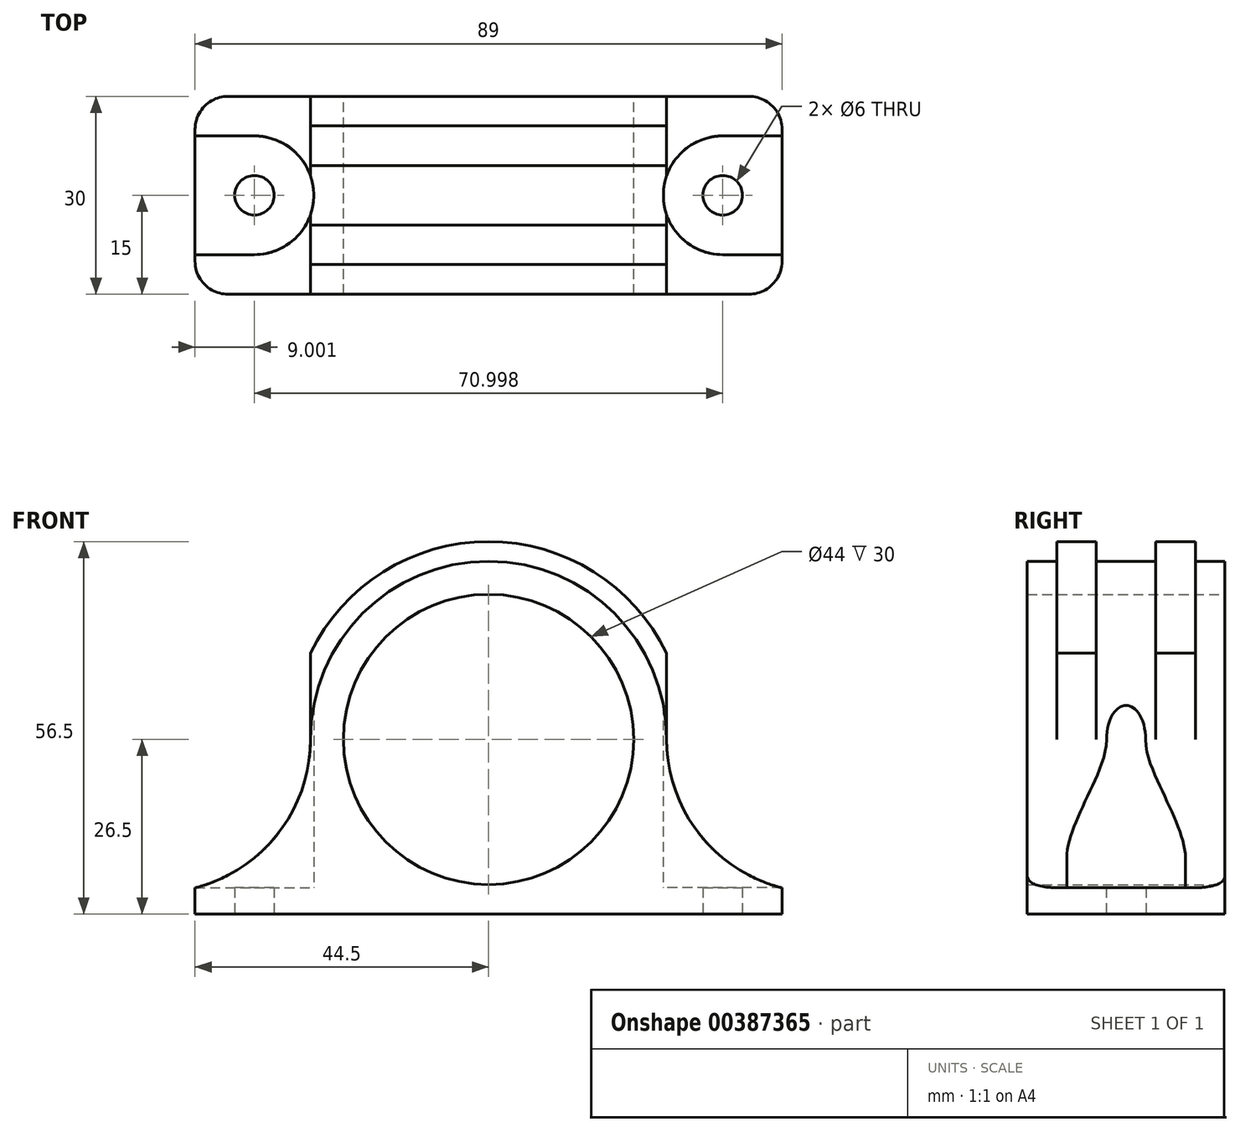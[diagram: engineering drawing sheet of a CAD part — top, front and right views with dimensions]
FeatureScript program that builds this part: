
annotation { "Feature Type Name" : "Feature", "Feature Type Description" : "" }
export const myFeature = defineFeature(function(context is Context, id is Id, definition is map)
    precondition{}
    {
        {
            var Q0;
            Q0=qCreatedBy(makeId("Front.planeOp"),FACE);
            var sketch = newSketch(context, id + "F0", { "sketchPlane" : qUnion([Q0])});
            skPoint(sketch, "E0", {"position": v(0, 0) * mm});
            skLineSegment(sketch, "E1", {"start": v(0, 0) * mm, "end": v(0, -26.5) * mm, "construction": true});
            skLineSegment(sketch, "E2", {"start": v(0, -26.5) * mm, "end": v(35.5, -26.5) * mm, "construction": true});
            skCircle(sketch, "E3", {"center": v(0, 0) * mm, "radius": 22 * mm, "construction": true});
            skLineSegment(sketch, "E4", {"start": v(35.5, -26.5) * mm, "end": v(44.5, -26.5) * mm, "construction": true});
            skLineSegment(sketch, "E5", {"start": v(44.5, -26.5) * mm, "end": v(0, -26.5) * mm});
            skLineSegment(sketch, "E6", {"start": v(35.5, -26.5) * mm, "end": v(26.5, -26.5) * mm, "construction": true});
            skArc(sketch, "E7", {"start": v(0, 22) * mm, "mid": v(22, 0) * mm, "end": v(0, -22) * mm});
            skLineSegment(sketch, "E8", {"start": v(0, -26.5) * mm, "end": v(0, -22) * mm});
            skLineSegment(sketch, "E9", {"start": v(44.5, -26.5) * mm, "end": v(44.5, -24.5) * mm, "construction": true});
            skLineSegment(sketch, "E10", {"start": v(44.5, -26.5) * mm, "end": v(44.5, -24.5) * mm});
            skPoint(sketch, "E11.snap10", {"position": v(17.75, -26.5) * mm});
            skLineSegment(sketch, "E12", {"start": v(44.5, -24.5) * mm, "end": v(44.5, -22.5) * mm});
            skLineSegment(sketch, "E13", {"start": v(0, 22) * mm, "end": v(0, 27) * mm, "construction": true});
            skPoint(sketch, "E14", {"position": v(0, 24.5) * mm});
            skArc(sketch, "E15", {"start": v(0, 27) * mm, "mid": v(25.85, 7.8) * mm, "end": v(14.92, -22.5) * mm, "construction": true});
            skLineSegment(sketch, "E16", {"start": v(22, 0) * mm, "end": v(24.5, 0) * mm, "construction": true});
            skArc(sketch, "E17", {"start": v(0, 27) * mm, "mid": v(19.1, 19.1) * mm, "end": v(27, 0) * mm});
            skLineSegment(sketch, "E18", {"start": v(22, 0) * mm, "end": v(24.5, 0) * mm});
            skLineSegment(sketch, "E19", {"start": v(24.5, 0) * mm, "end": v(24.5, -24.5) * mm});
            skLineSegment(sketch, "E20", {"start": v(24.5, -24.5) * mm, "end": v(44.5, -24.5) * mm});
            skLineSegment(sketch, "E21", {"start": v(44.5, -22.5) * mm, "end": v(24.5, -22.5) * mm, "construction": true});
            skLineSegment(sketch, "E22", {"start": v(27, 0) * mm, "end": v(27, -22.5) * mm});
            skLineSegment(sketch, "E23", {"start": v(27, -22.5) * mm, "end": v(44.5, -22.5) * mm});
            skLineSegment(sketch, "E24", {"start": v(0, 27) * mm, "end": v(0, 22) * mm});
            skArc(sketch, "E25", {"start": v(27, 0) * mm, "mid": v(31.9, -14.25) * mm, "end": v(44.5, -22.5) * mm});
            skSolve(sketch);
        }
        {
            var Q0;
            Q0=makeQuery(id+"F0.imprint","IMPRINT",FACE,{"disambiguationData":[TD([[makeQuery(id+"F0.imprint","IMPRINT",EDGE,{"derivedFrom":sQuery(id+"F0.wireOp",EDGE,"E5")}),-1.0]])]});
            extrude(context, id + "F1", {"entities" : qUnion([Q0]), "depth" : 15 * mm, "offsetDistance" : 25 * mm, "hasSecondDirection" : true, "secondDirectionOppositeDirection" : true, "secondDirectionDepth" : 15 * mm});
        }
        {
            var Q0;
            Q0=makeQuery(id+"F0.imprint","IMPRINT",FACE,{"disambiguationData":[TD([[makeQuery(id+"F0.imprint","IMPRINT",EDGE,{"derivedFrom":sQuery(id+"F0.wireOp",EDGE,"E12")}),1.0]])]});
            var Q1;
            Q1=makeQuery(id+"F0.imprint","IMPRINT",FACE,{"disambiguationData":[TD([[makeQuery(id+"F0.imprint","IMPRINT",EDGE,{"derivedFrom":sQuery(id+"F0.wireOp",EDGE,"E22")}),1.0]])]});
            extrude(context, id + "F2", {"entities" : qUnion([Q0, Q1]), "depth" : 15 * mm, "offsetDistance" : 25 * mm, "hasSecondDirection" : true, "secondDirectionOppositeDirection" : true, "secondDirectionDepth" : 15 * mm});
        }
        {
            var Q0;
            Q0=makeQuery(id+"F1.opExtrude","SWEPT_FACE",FACE,{"disambiguationData":[OSD([sQuery(id+"F0.wireOp",EDGE,"E5")])]});
            var sketch = newSketch(context, id + "F3", { "sketchPlane" : qUnion([Q0])});
            skPoint(sketch, "E26", {"position": v(35.5, 0) * mm});
            skPoint(sketch, "E26.positionSnap0", {"position": v(44.5, 0) * mm});
            skCircle(sketch, "E27", {"center": v(35.5, 0) * mm, "radius": 3 * mm});
            skSolve(sketch);
        }
        {
            var Q0;
            Q0=makeQuery(id+"F3.imprint","IMPRINT",FACE,{"disambiguationData":[TD([[makeQuery(id+"F3.imprint","IMPRINT",EDGE,{"derivedFrom":sQuery(id+"F3.wireOp",EDGE,"E27")}),1.0]])]});
            extrude(context, id + "F4", {"entities" : qUnion([Q0]), "operationType" : NewBodyOperationType.REMOVE, "endBound" : BoundingType.THROUGH_ALL, "oppositeDirection" : true, "depth" : 25 * mm, "offsetDistance" : 25 * mm});
        }
        {
            var Q0;
            Q0=makeQuery(id+"F1.opExtrude","SWEPT_BODY",BODY,{"disambiguationData":[OSD([sQuery(id+"F0.wireOp",EDGE,"E5"),sQuery(id+"F0.wireOp",EDGE,"E7"),sQuery(id+"F0.wireOp",EDGE,"oa173LJA-7Qzk-bxVo-JVOY-SVkXLDIxbrzX"),sQuery(id+"F0.wireOp",EDGE,"oVmq41rx-Tf5Z-87iy-jocJ-56lhmhOnJXAm"),sQuery(id+"F0.wireOp",EDGE,"17kKks0d-jc19-QXFi-ibKR-wiCfBObhO1gz"),sQuery(id+"F0.wireOp",EDGE,"E8"),sQuery(id+"F0.wireOp",EDGE,"bDHaJZQo-ug9d-Zn0I-X4ck-lXPpdy3Wryym"),sQuery(id+"F0.wireOp",EDGE,"E10"),sQuery(id+"F0.wireOp",EDGE,"ApmxlAoO-5xRw-mKMb-g5nd-2PpKJuiYlqXn"),sQuery(id+"F0.wireOp",EDGE,"E11")])]});
            var Q1;
            Q1=qCreatedBy(makeId("Right.planeOp"),FACE);
            mirror(context, id + "F5", {"operationType" : NewBodyOperationType.ADD, "entities" : qUnion([Q0]), "mirrorPlane" : qUnion([Q1])});
        }
        {
            var Q0;
            {var subQ0=makeQuery(id+"F1.opExtrude","SWEPT_FACE",FACE,{"disambiguationData":[OSD([sQuery(id+"F0.wireOp",EDGE,"E5")])]});Q0=makeQuery(id+"F5.boolean.opBoolean","MERGE",FACE,{"derivedFrom":[subQ0,makeQuery(id+"F5.opPattern","COPY",FACE,{"derivedFrom":subQ0,"instanceName":"1"})]});}
            var sketch = newSketch(context, id + "F6", { "sketchPlane" : qUnion([Q0])});
            skPoint(sketch, "E28", {"position": v(35.5, 0) * mm});
            skLineSegment(sketch, "E29", {"start": v(35.5, 0) * mm, "end": v(26.5, 0) * mm, "construction": true});
            skPoint(sketch, "E30", {"position": v(31.38, 15) * mm});
            skPoint(sketch, "E31", {"position": v(31.38, -15) * mm});
            skLineSegment(sketch, "E32", {"start": v(44.5, 15) * mm, "end": v(44.5, -15) * mm});
            skCircle(sketch, "E33", {"center": v(35.5, 0) * mm, "radius": 9 * mm, "construction": true});
            skLineSegment(sketch, "E34", {"start": v(35.5, 0) * mm, "end": v(35.5, 9) * mm, "construction": true});
            skLineSegment(sketch, "E35", {"start": v(35.5, 0) * mm, "end": v(35.5, -9) * mm, "construction": true});
            skArc(sketch, "E36", {"start": v(35.5, 9) * mm, "mid": v(26.5, 0) * mm, "end": v(35.5, -9) * mm});
            skLineSegment(sketch, "E37", {"start": v(35.5, -9) * mm, "end": v(44.5, -9) * mm});
            skLineSegment(sketch, "E38", {"start": v(44.5, -9) * mm, "end": v(44.5, 9) * mm});
            skLineSegment(sketch, "E39", {"start": v(44.5, 9) * mm, "end": v(35.5, 9) * mm});
            skSolve(sketch);
        }
        {
            var Q0;
            Q0=makeQuery(id+"F6.imprint","IMPRINT",FACE,{"disambiguationData":[TD([[makeQuery(id+"F6.imprint","IMPRINT",EDGE,{"derivedFrom":sQuery(id+"F6.wireOp",EDGE,"E36")}),1.0]])]});
            extrude(context, id + "F7", {"entities" : qUnion([Q0]), "operationType" : NewBodyOperationType.REMOVE, "oppositeDirection" : true, "depth" : 40 * mm, "offsetDistance" : 25 * mm, "hasSecondDirection" : true, "secondDirectionOppositeDirection" : true, "secondDirectionDepth" : 4 * mm});
        }
        {
            var Q0;
            Q0=makeQuery(id+"F2.opExtrude","SWEPT_BODY",BODY,{"disambiguationData":[OSD([sQuery(id+"F0.wireOp",EDGE,"E7"),sQuery(id+"F0.wireOp",EDGE,"E12"),sQuery(id+"F0.wireOp",EDGE,"E17"),sQuery(id+"F0.wireOp",EDGE,"E18"),sQuery(id+"F0.wireOp",EDGE,"E19"),sQuery(id+"F0.wireOp",EDGE,"E20"),sQuery(id+"F0.wireOp",EDGE,"E24"),sQuery(id+"F0.wireOp",EDGE,"E25")])]});
            var Q1;
            Q1=qCreatedBy(makeId("Right.planeOp"),FACE);
            mirror(context, id + "F8", {"operationType" : NewBodyOperationType.ADD, "entities" : qUnion([Q0]), "mirrorPlane" : qUnion([Q1])});
        }
        {
            var Q0;
            Q0=qCreatedBy(makeId("Right.planeOp"),FACE);
            var sketch = newSketch(context, id + "F9", { "sketchPlane" : qUnion([Q0])});
            skLineSegment(sketch, "E40", {"start": v(0, 0) * mm, "end": v(15, 0) * mm, "construction": true});
            skLineSegment(sketch, "E41", {"start": v(15, 0) * mm, "end": v(15, 27) * mm, "construction": true});
            skLineSegment(sketch, "E42", {"start": v(0, 0) * mm, "end": v(7.5, 0) * mm, "construction": true});
            skLineSegment(sketch, "E43", {"start": v(7.5, 0) * mm, "end": v(10.5, 0) * mm, "construction": true});
            skLineSegment(sketch, "E44", {"start": v(10.5, 0) * mm, "end": v(10.5, 27) * mm, "construction": true});
            skLineSegment(sketch, "E45", {"start": v(10.5, 27) * mm, "end": v(4.5, 27) * mm, "construction": true});
            skLineSegment(sketch, "E46", {"start": v(4.5, 27) * mm, "end": v(4.5, 0) * mm, "construction": true});
            skLineSegment(sketch, "E47", {"start": v(4.5, 27) * mm, "end": v(4.5, 30) * mm, "construction": true});
            skLineSegment(sketch, "E48", {"start": v(4.5, 30) * mm, "end": v(10.5, 30) * mm, "construction": true});
            skLineSegment(sketch, "E49", {"start": v(10.5, 30) * mm, "end": v(10.5, 27) * mm, "construction": true});
            skLineSegment(sketch, "E50.bottom", {"start": v(4.5, 30) * mm, "end": v(10.5, 30) * mm});
            skLineSegment(sketch, "E50.top", {"start": v(4.5, 0) * mm, "end": v(10.5, 0) * mm});
            skLineSegment(sketch, "E50.left", {"start": v(4.5, 30) * mm, "end": v(4.5, 0) * mm});
            skLineSegment(sketch, "E50.right", {"start": v(10.5, 30) * mm, "end": v(10.5, 0) * mm});
            skLineSegment(sketch, "E51", {"start": v(0, 0) * mm, "end": v(-7.5, 0) * mm, "construction": true});
            skLineSegment(sketch, "E52", {"start": v(-7.5, 0) * mm, "end": v(-10.5, 0) * mm, "construction": true});
            skLineSegment(sketch, "E53", {"start": v(-10.5, 0) * mm, "end": v(-10.5, 30) * mm, "construction": true});
            skLineSegment(sketch, "E54", {"start": v(-10.5, 30) * mm, "end": v(-4.5, 30) * mm, "construction": true});
            skLineSegment(sketch, "E55", {"start": v(-4.5, 30) * mm, "end": v(-4.5, 0) * mm, "construction": true});
            skLineSegment(sketch, "E56.bottom", {"start": v(-10.5, 30) * mm, "end": v(-4.5, 30) * mm});
            skLineSegment(sketch, "E56.top", {"start": v(-10.5, 0) * mm, "end": v(-4.5, 0) * mm});
            skLineSegment(sketch, "E56.left", {"start": v(-10.5, 30) * mm, "end": v(-10.5, 0) * mm});
            skLineSegment(sketch, "E56.right", {"start": v(-4.5, 30) * mm, "end": v(-4.5, 0) * mm});
            skSolve(sketch);
        }
        {
            var Q0;
            Q0 = qSketchRegion(id + "F9", true);
            extrude(context, id + "F10", {"entities" : qUnion([Q0]), "operationType" : NewBodyOperationType.ADD, "depth" : 27 * mm, "offsetDistance" : 25 * mm, "hasSecondDirection" : true, "secondDirectionOppositeDirection" : true, "secondDirectionDepth" : 27 * mm});
        }
        {
            var Q0;
            Q0=qCreatedBy(makeId("Front.planeOp"),FACE);
            var sketch = newSketch(context, id + "F11", { "sketchPlane" : qUnion([Q0])});
            skCircle(sketch, "E57", {"center": v(0, 0) * mm, "radius": 22 * mm});
            skLineSegment(sketch, "E58", {"start": v(0, 0) * mm, "end": v(27, 0) * mm, "construction": true});
            skLineSegment(sketch, "E59", {"start": v(0, 0) * mm, "end": v(-27, 0) * mm, "construction": true});
            skLineSegment(sketch, "E60", {"start": v(0, 0) * mm, "end": v(42, 0) * mm, "construction": true});
            skArc(sketch, "E61", {"start": v(42, 0) * mm, "mid": v(0, 42) * mm, "end": v(-42, 0) * mm});
            skLineSegment(sketch, "E62", {"start": v(-27, 0) * mm, "end": v(0, 0) * mm, "construction": true});
            skPoint(sketch, "E63", {"position": v(-27, 0) * mm});
            skPoint(sketch, "E64", {"position": v(27, 0) * mm});
            skLineSegment(sketch, "E65", {"start": v(-27, 0) * mm, "end": v(-30, 0) * mm, "construction": true});
            skLineSegment(sketch, "E66", {"start": v(27, 0) * mm, "end": v(30, 0) * mm, "construction": true});
            skArc(sketch, "E67", {"start": v(-30, 0) * mm, "mid": v(0, 30) * mm, "end": v(30, 0) * mm});
            skLineSegment(sketch, "E68", {"start": v(-42, 0) * mm, "end": v(-30, 0) * mm});
            skLineSegment(sketch, "E69", {"start": v(30, 0) * mm, "end": v(42, 0) * mm});
            skSolve(sketch);
        }
        {
            var Q0;
            Q0=makeQuery(id+"F5.opPattern","COPY",EDGE,{"derivedFrom":makeQuery(id+"F1.opExtrude","CAP_EDGE",EDGE,{"disambiguationData":[OSD([sQuery(id+"F0.wireOp",EDGE,"E10")])],"isStart":true}),"instanceName":"1"});
            var Q1;
            Q1=makeQuery(id+"F8.opPattern","COPY",EDGE,{"derivedFrom":makeQuery(id+"F2.opExtrude","CAP_EDGE",EDGE,{"disambiguationData":[OSD([sQuery(id+"F0.wireOp",EDGE,"E12")])],"isStart":true}),"instanceName":"1"});
            var Q2;
            Q2=makeQuery(id+"F5.opPattern","COPY",EDGE,{"derivedFrom":makeQuery(id+"F1.opExtrude","CAP_EDGE",EDGE,{"disambiguationData":[OSD([sQuery(id+"F0.wireOp",EDGE,"E10")])],"isStart":false}),"instanceName":"1"});
            var Q3;
            Q3=makeQuery(id+"F8.opPattern","COPY",EDGE,{"derivedFrom":makeQuery(id+"F2.opExtrude","CAP_EDGE",EDGE,{"disambiguationData":[OSD([sQuery(id+"F0.wireOp",EDGE,"E12")])],"isStart":false}),"instanceName":"1"});
            var Q4;
            Q4=makeQuery(id+"F1.opExtrude","CAP_EDGE",EDGE,{"disambiguationData":[OSD([sQuery(id+"F0.wireOp",EDGE,"E10")])],"isStart":false});
            var Q5;
            Q5=makeQuery(id+"F2.opExtrude","CAP_EDGE",EDGE,{"disambiguationData":[OSD([sQuery(id+"F0.wireOp",EDGE,"E12")])],"isStart":false});
            var Q6;
            Q6=makeQuery(id+"F1.opExtrude","CAP_EDGE",EDGE,{"disambiguationData":[OSD([sQuery(id+"F0.wireOp",EDGE,"E10")])],"isStart":true});
            var Q7;
            Q7=makeQuery(id+"F2.opExtrude","CAP_EDGE",EDGE,{"disambiguationData":[OSD([sQuery(id+"F0.wireOp",EDGE,"E12")])],"isStart":true});
            fillet(context, id + "F12", {"entities" : qUnion([Q0, Q1, Q2, Q3, Q4, Q5, Q6, Q7]), "radius" : 5 * mm, "tangentPropagation" : true, "allowEdgeOverflow" : false});
        }
        {
            var Q0;
            Q0=makeQuery(id+"F11.imprint","IMPRINT",FACE,{"disambiguationData":[TD([[makeQuery(id+"F11.imprint","IMPRINT",EDGE,{"derivedFrom":sQuery(id+"F11.wireOp",EDGE,"E61")}),1.0]])]});
            var Q1;
            Q1=makeQuery(id+"F11.imprint","IMPRINT",FACE,{"disambiguationData":[TD([[makeQuery(id+"F11.imprint","IMPRINT",EDGE,{"derivedFrom":sQuery(id+"F11.wireOp",EDGE,"E57")}),1.0]])]});
            extrude(context, id + "F13", {"entities" : qUnion([Q0, Q1]), "operationType" : NewBodyOperationType.REMOVE, "oppositeDirection" : true, "depth" : 25 * mm, "offsetDistance" : 25 * mm, "hasSecondDirection" : true, "secondDirectionOppositeDirection" : false, "secondDirectionDepth" : 25 * mm});
        }
    });
